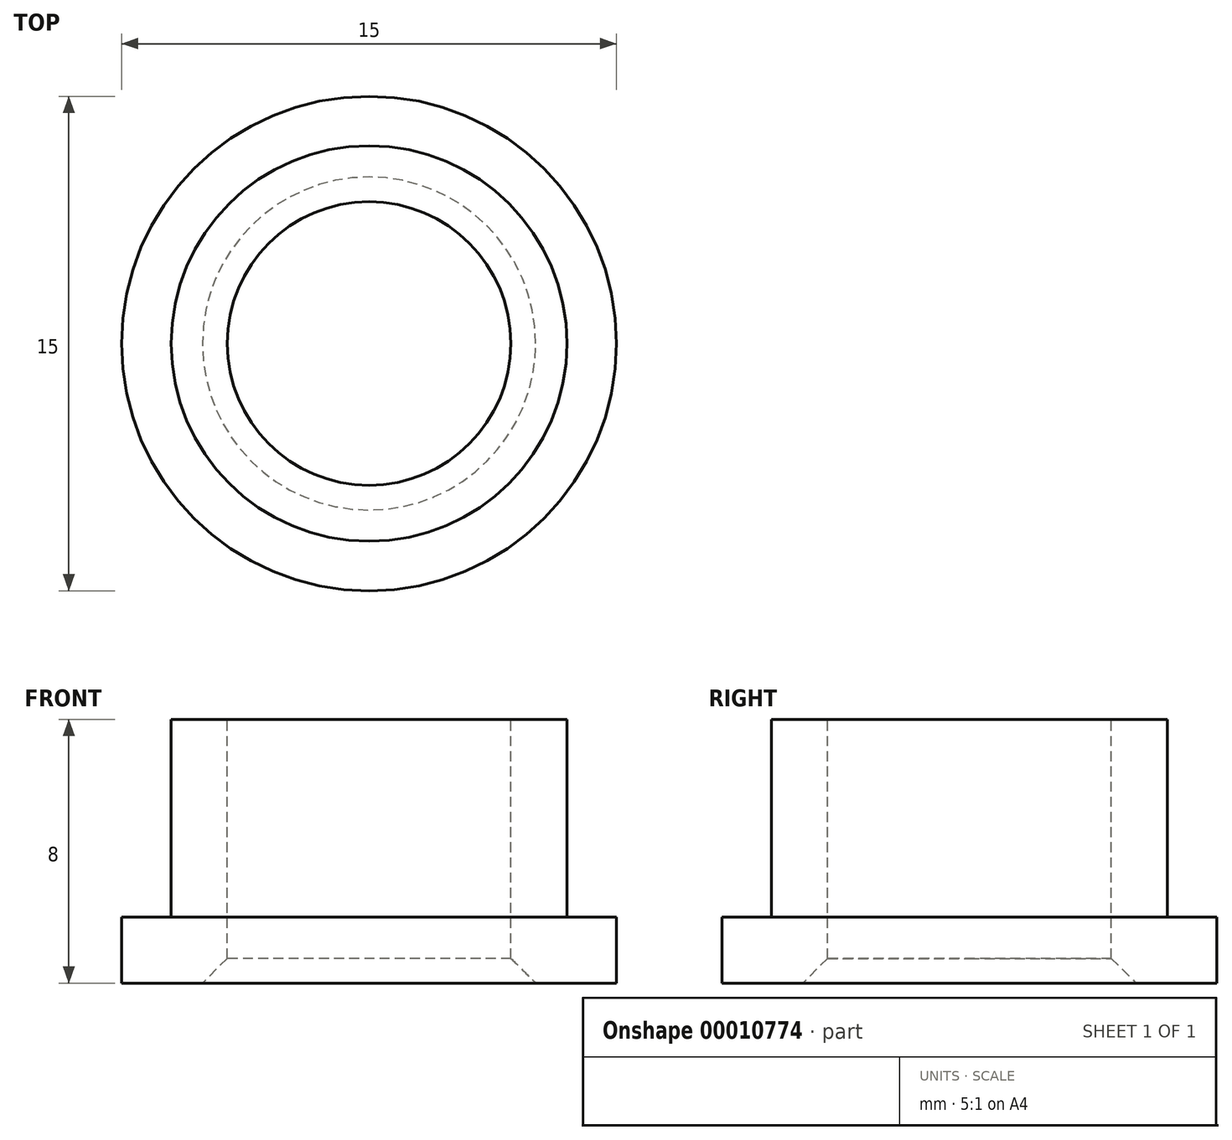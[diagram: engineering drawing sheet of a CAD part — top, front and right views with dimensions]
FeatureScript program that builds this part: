
annotation { "Feature Type Name" : "Feature", "Feature Type Description" : "" }
export const myFeature = defineFeature(function(context is Context, id is Id, definition is map)
    precondition{}
    {
        {
            var Q0;
            Q0=qCreatedBy(makeId("Top.planeOp"),FACE);
            var sketch = newSketch(context, id + "F0", { "sketchPlane" : qUnion([Q0])});
            skCircle(sketch, "E0", {"center": v(0, 0) * mm, "radius": 7.5 * mm});
            skSolve(sketch);
        }
        {
            var Q0;
            Q0 = qSketchRegion(id + "F0", true);
            extrude(context, id + "F1", {"entities" : qUnion([Q0]), "depth" : 2 * mm});
        }
        {
            var Q0;
            Q0=makeQuery(id+"F1.opExtrude","CAP_FACE",FACE,{"disambiguationData":[OSD([sQuery(id+"F0.wireOp",EDGE,"E0")])],"isStart":false});
            var sketch = newSketch(context, id + "F2", { "sketchPlane" : qUnion([Q0])});
            skCircle(sketch, "E1", {"center": v(0, 0) * mm, "radius": 6 * mm});
            skSolve(sketch);
        }
        {
            var Q0;
            Q0 = qSketchRegion(id + "F2", true);
            extrude(context, id + "F3", {"entities" : qUnion([Q0]), "operationType" : NewBodyOperationType.ADD, "depth" : 6 * mm});
        }
        {
            var Q0;
            Q0=makeQuery(id+"F3.opExtrude","CAP_FACE",FACE,{"disambiguationData":[OSD([sQuery(id+"F2.wireOp",EDGE,"E1")])],"isStart":false});
            var sketch = newSketch(context, id + "F4", { "sketchPlane" : qUnion([Q0])});
            skCircle(sketch, "E2", {"center": v(0, 0) * mm, "radius": 4.3 * mm});
            skSolve(sketch);
        }
        {
            var Q0;
            Q0 = qSketchRegion(id + "F4", true);
            extrude(context, id + "F5", {"entities" : qUnion([Q0]), "operationType" : NewBodyOperationType.REMOVE, "oppositeDirection" : true, "depth" : 25 * mm});
        }
        {
            var Q0;
            Q0=makeQuery(id+"F5.boolean.opBoolean","COPY",EDGE,{"derivedFrom":makeQuery(id+"F5.opExtrude","CAP_EDGE",EDGE,{"disambiguationData":[OSD([sQuery(id+"F4.wireOp",EDGE,"E2")])],"isStart":true})});
            var Q1;
            Q1=makeQuery(id+"F5.boolean.opBoolean","INTERSECT",EDGE,{"derivedFrom":[makeQuery(id+"F1.opExtrude","CAP_FACE",FACE,{"disambiguationData":[OSD([sQuery(id+"F0.wireOp",EDGE,"E0")])],"isStart":true}),makeQuery(id+"F5.opExtrude","SWEPT_FACE",FACE,{"disambiguationData":[OSD([sQuery(id+"F4.wireOp",EDGE,"E2")])]})]});
            chamfer(context, id + "F6", {"entities" : qUnion([Q0, Q1]), "width" : .75 * mm, "tangentPropagation" : true});
        }
    });
